# Revit family: Drinking_Fountain-Haws_Corporation-Wall_Mounted_1117NL
name_source: partatom
category: Plumbing Fixtures
revit_build: Autodesk Revit 2016 (Build: 20150220_1215(x64)
units: mm (PartAtom-declared; Revit-internal decimal feet)

## family parameters
Always vertical = Yes
Cut with Voids When Loaded = No
Host = Wall
OmniClass Number = 23.65.70.14.11
OmniClass Title = Drinking Fountains/Coolers
Part Type = Normal
Room Calculation Point = No
Round Connector Dimension = Use Radius
Shared = Yes

## types (1)
- 1117NL
    Assembly Code = D2010810
    BIMobject category = Taps & Mixers
    BIMobject category code = sanitary-taps-mixers
    BIMobject main category = Sanitary
    BIMobject main category code = sanitary
    Back Panel = Metal - Haws Corporation - Satin Stainless Steel
    Basin Height = 4 1/4"
    Basin Width = 12"
    Beep Level = 0"
    Bowl = Metal - Haws Corporation - Satin Stainless Steel
    Brand url = https://www.hawsco.com
    CW Connection = Yes
    CWFU = 1
    Cost = $0
    Cost Note = For Cost information please visit the Resource tab in the Product Page URL
    Date of publishing = 6/4/2019
    Description = "Hi-Lo" adjustable design allows for twice the users as regular fountains and suits the needs for various user heights
    Design country = United States
    EAN code = https://611970317304
    Edition number = 1
    Flow = 0.00 GPM
    HW Connection = No
    HWFU = 0
    Installation instructions = http://www.hawsco.com
    Keynote = 15410.A1
    Manufacturer = Haws Corporation 1455 Kleppe Lane Sparks, NV 89431
    Manufacturer country = United States
    Manufacturer name = Haws Corporation
    Masterformat 2014 Code = 22 47 13
    Masterformat 2014 Description = Drinking Fountains
    Material main = Metal
    Model = 1117L
    Nominal height = 16"
    Nominal width = 32"
    OmniClass Code = 23-31 31 00
    OmniClass Description = Drinking Fountains
    Product Documentation Link = http://www.hawsco.com
    Product Guid = 4bf674c3-3775-4760-8085-55f44b9d5ad0
    Product Page URL = http://www.hawsco.com
    Product SKU = haws-1117LN
    Product certification = http://www.csagroup.org
    Product data url = https://bimobject.com
    Product family = Drinking Fountains/Coolers
    Product group = Wall Mounted Drinking Fountains
    Product url = http://www.hawsco.com
    Sanitary Radius = 5/8"
    Series = The Haws 1117 adjustable barrier free Hi-Lo drinking fountain
    Supply Radius = 1/4"
    Technical description = http://www.hawsco.com
    Trim = Metal - Haws Corporation - Satin Stainless Steel
    Tubing = Metal - Haws Corporation - Copper Poly
    Type Comments = "Hi-Lo" drinking fountain with antimicrobial protection* uses a patented push-button valve assembly
    URL = http://www.hawsco.com
    Uniclass 2015 Code = Pr_40_20_87_24
    Uniclass 2015 Name = Drinking fountains
    Vent Connection = Yes
    WFU = 1
    Waste Connection = Yes
    Weight Net (Kg) = 71

## geometry (parser evidence)
native form markers: Sweep x5
no freeform markers — native parametric forms only
